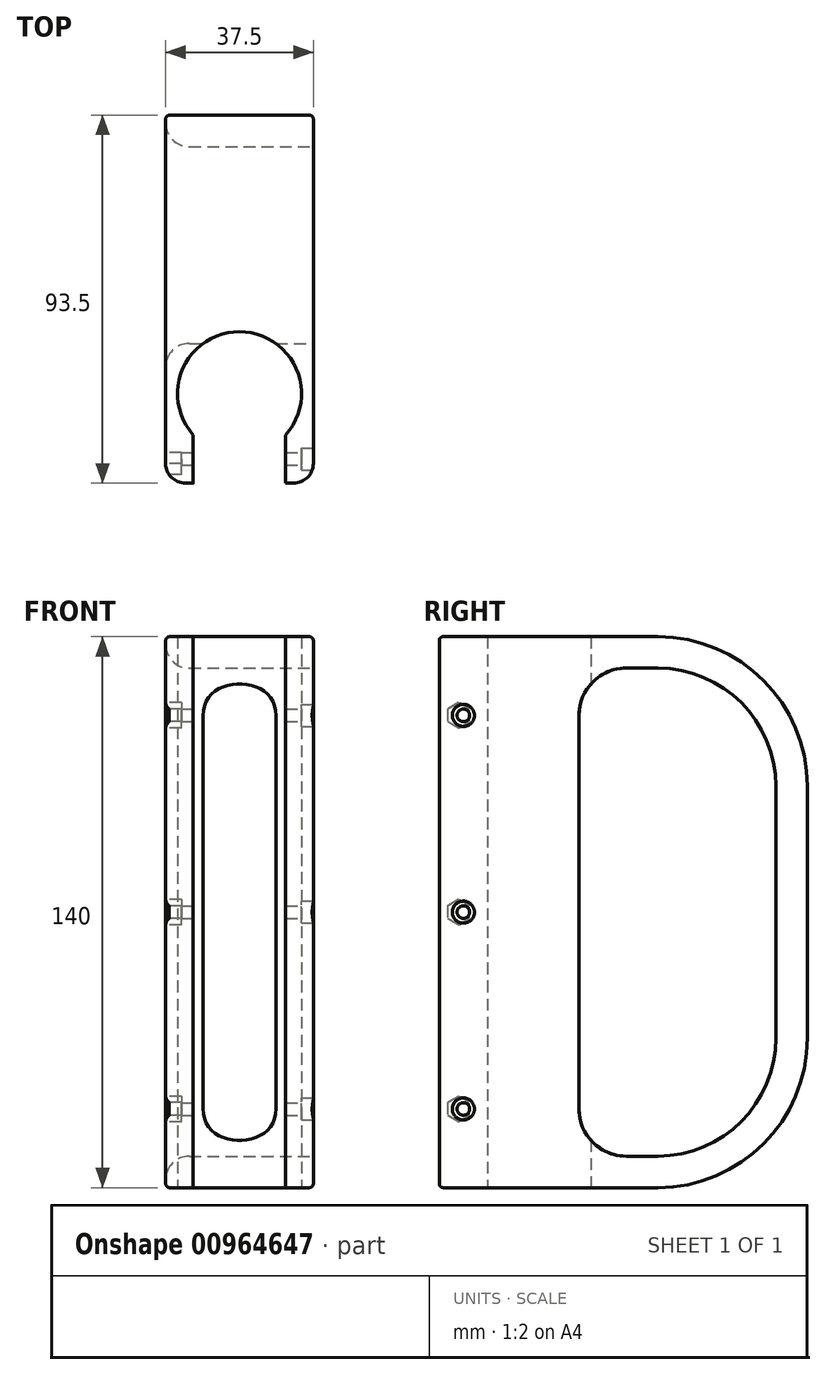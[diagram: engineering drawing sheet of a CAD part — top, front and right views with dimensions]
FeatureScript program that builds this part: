
annotation { "Feature Type Name" : "Feature", "Feature Type Description" : "" }
export const myFeature = defineFeature(function(context is Context, id is Id, definition is map)
    precondition{}
    {
        {
            var Q0;
            Q0=qCreatedBy(makeId("Top.planeOp"),FACE);
            var sketch = newSketch(context, id + "F0", { "sketchPlane" : qUnion([Q0])});
            skCircle(sketch, "E0", {"center": v(0, 0) * mm, "radius": 15.75 * mm});
            skSolve(sketch);
        }
        {
            var Q0;
            Q0=qCreatedBy(makeId("Top.planeOp"),FACE);
            var sketch = newSketch(context, id + "F1", { "sketchPlane" : qUnion([Q0])});
            skLineSegment(sketch, "E1", {"start": v(0, 70.75) * mm, "end": v(18.75, 70.75) * mm});
            skLineSegment(sketch, "E2", {"start": v(18.75, 70.75) * mm, "end": v(18.75, -22.75) * mm});
            skLineSegment(sketch, "E3", {"start": v(18.75, -22.75) * mm, "end": v(11.75, -22.75) * mm});
            skLineSegment(sketch, "E4", {"start": v(11.75, -22.75) * mm, "end": v(11.75, -10.49) * mm});
            skArc(sketch, "E5", {"start": v(11.75, -10.49) * mm, "mid": v(14.37, 6.44) * mm, "end": v(0, 15.75) * mm});
            skLineSegment(sketch, "E6", {"start": v(0, 15.75) * mm, "end": v(0, 70.75) * mm});
            skLineSegment(sketch, "E7", {"start": v(15.75, 0) * mm, "end": v(15.75, -22.75) * mm, "construction": true});
            skLineSegment(sketch, "E8", {"start": v(0, -15.75) * mm, "end": v(11.75, -15.75) * mm, "construction": true});
            skSolve(sketch);
        }
        {
            var Q0;
            Q0=makeQuery(id+"F1.imprint","IMPRINT",FACE,{"disambiguationData":[TD([[makeQuery(id+"F1.imprint","IMPRINT",EDGE,{"derivedFrom":sQuery(id+"F1.wireOp",EDGE,"E1")}),-1.0]])]});
            extrude(context, id + "F2", {"entities" : qUnion([Q0]), "depth" : 70 * mm});
        }
        {
            var Q0;
            Q0=makeQuery(id+"F2.opExtrude","SWEPT_BODY",BODY,{"disambiguationData":[OSD([sQuery(id+"F1.wireOp",EDGE,"E1"),sQuery(id+"F1.wireOp",EDGE,"E2"),sQuery(id+"F1.wireOp",EDGE,"E3"),sQuery(id+"F1.wireOp",EDGE,"E4"),sQuery(id+"F1.wireOp",EDGE,"E5"),sQuery(id+"F1.wireOp",EDGE,"E6")])]});
            var Q1;
            Q1=makeQuery(id+"F2.opExtrude","SWEPT_FACE",FACE,{"disambiguationData":[OSD([sQuery(id+"F1.wireOp",EDGE,"E6")])]});
            mirror(context, id + "F3", {"operationType" : NewBodyOperationType.ADD, "entities" : qUnion([Q0]), "mirrorPlane" : qUnion([Q1])});
        }
        {
            var Q0;
            Q0=makeQuery(id+"F2.opExtrude","SWEPT_FACE",FACE,{"disambiguationData":[OSD([sQuery(id+"F1.wireOp",EDGE,"E2")])]});
            var sketch = newSketch(context, id + "F4", { "sketchPlane" : qUnion([Q0])});
            skLineSegment(sketch, "E9", {"start": v(62.75, 70) * mm, "end": v(62.75, 38) * mm});
            skLineSegment(sketch, "E10", {"start": v(12.75, 20) * mm, "end": v(12.75, 70) * mm});
            skLineSegment(sketch, "E11", {"start": v(62.75, 70) * mm, "end": v(12.75, 70) * mm});
            skLineSegment(sketch, "E12", {"start": v(15.75, 70) * mm, "end": v(15.75, 0) * mm, "construction": true});
            skLineSegment(sketch, "E13", {"start": v(70.75, 8) * mm, "end": v(15.75, 8) * mm, "construction": true});
            skLineSegment(sketch, "E14", {"start": v(32.75, 8) * mm, "end": v(24.75, 8) * mm});
            skArc(sketch, "E15", {"start": v(12.75, 20) * mm, "mid": v(16.26, 11.51) * mm, "end": v(24.75, 8) * mm});
            skArc(sketch, "E16", {"start": v(32.75, 8) * mm, "mid": v(53.96, 16.79) * mm, "end": v(62.75, 38) * mm});
            skSolve(sketch);
        }
        {
            var Q0;
            Q0=qSketchRegion(id+"F4",true);
            var Q1;
            {var subQ2=sQuery(id+"F4.wireOp",EDGE,"E11");Q1=makeQuery(id+"F4.imprint","IMPRINT",FACE,{"disambiguationData":[TD([[makeQuery(id+"F4.imprint","IMPRINT",EDGE,{"derivedFrom":subQ2}),1.0]])]});}
            extrude(context, id + "F5", {"entities" : qUnion([Q0, Q1]), "operationType" : NewBodyOperationType.REMOVE, "endBound" : BoundingType.THROUGH_ALL, "oppositeDirection" : true, "depth" : 25 * mm});
        }
        {
            var Q0;
            {var subQ0=makeQuery(id+"F2.opExtrude","SWEPT_FACE",FACE,{"disambiguationData":[OSD([sQuery(id+"F1.wireOp",EDGE,"E2")])]});Q0=makeQuery(id+"F8.boolean.opBoolean","MERGE",FACE,{"derivedFrom":[subQ0,makeQuery(id+"F8.opPattern","COPY",FACE,{"derivedFrom":subQ0,"instanceName":"1"})]});}
            var sketch = newSketch(context, id + "F6", { "sketchPlane" : qUnion([Q0])});
            skArc(sketch, "E17", {"start": v(32.75, 0) * mm, "mid": v(59.62, 11.13) * mm, "end": v(70.75, 38) * mm});
            skLineSegment(sketch, "E18", {"start": v(70.75, 38) * mm, "end": v(70.75, 0) * mm});
            skLineSegment(sketch, "E19", {"start": v(70.75, 0) * mm, "end": v(32.75, 0) * mm});
            skSolve(sketch);
        }
        {
            var Q0;
            Q0=qSketchRegion(id+"F6",true);
            extrude(context, id + "F7", {"entities" : qUnion([Q0]), "operationType" : NewBodyOperationType.REMOVE, "endBound" : BoundingType.THROUGH_ALL, "oppositeDirection" : true, "depth" : 25 * mm});
        }
        {
            var Q0;
            Q0=makeQuery(id+"F2.opExtrude","SWEPT_BODY",BODY,{"disambiguationData":[OSD([sQuery(id+"F1.wireOp",EDGE,"E1"),sQuery(id+"F1.wireOp",EDGE,"E2"),sQuery(id+"F1.wireOp",EDGE,"E3"),sQuery(id+"F1.wireOp",EDGE,"E4"),sQuery(id+"F1.wireOp",EDGE,"E5"),sQuery(id+"F1.wireOp",EDGE,"E6")])]});
            var Q1;
            {var subQ0=sQuery(id+"F1.wireOp",EDGE,"E2");var subQ1=sQuery(id+"F1.wireOp",EDGE,"E3");var subQ2=sQuery(id+"F1.wireOp",EDGE,"E4");var subQ3=sQuery(id+"F1.wireOp",EDGE,"E5");var subQ4=makeQuery(id+"F2.opExtrude","CAP_FACE",FACE,{"disambiguationData":[OSD([sQuery(id+"F1.wireOp",EDGE,"E1"),subQ0,subQ1,subQ2,subQ3,sQuery(id+"F1.wireOp",EDGE,"E6")])],"isStart":false});var subQ6=makeQuery(id+"F2.opExtrude","SWEPT_FACE",FACE,{"disambiguationData":[OSD([subQ1])]});Q1=makeQuery(id+"F5.boolean.opBoolean","SPLIT",FACE,{"disambiguationData":[TD([subQ6])],"derivedFrom":makeQuery(id+"F3.boolean.opBoolean","MERGE",FACE,{"derivedFrom":[subQ4,makeQuery(id+"F3.opPattern","COPY",FACE,{"derivedFrom":subQ4,"instanceName":"1"})]})});}
            mirror(context, id + "F8", {"operationType" : NewBodyOperationType.ADD, "entities" : qUnion([Q0]), "mirrorPlane" : qUnion([Q1])});
        }
        {
            var Q0;
            {var subQ0=makeQuery(id+"F5.boolean.opBoolean","COPY",EDGE,{"derivedFrom":makeQuery(id+"F5.opExtrude","CAP_EDGE",EDGE,{"disambiguationData":[OSD([sQuery(id+"F4.wireOp",EDGE,"E10")])],"isStart":true})});Q0=makeQuery(id+"F8.boolean.opBoolean","MERGE",EDGE,{"derivedFrom":[subQ0,makeQuery(id+"F8.opPattern","COPY",EDGE,{"derivedFrom":subQ0,"instanceName":"1"})]});}
            var Q1;
            {var subQ0=makeQuery(id+"F5.boolean.opBoolean","INTERSECT",EDGE,{"derivedFrom":[makeQuery(id+"F3.opPattern","COPY",FACE,{"derivedFrom":makeQuery(id+"F2.opExtrude","SWEPT_FACE",FACE,{"disambiguationData":[OSD([sQuery(id+"F1.wireOp",EDGE,"E2")])]}),"instanceName":"1"}),makeQuery(id+"F5.opExtrude","SWEPT_FACE",FACE,{"disambiguationData":[OSD([sQuery(id+"F4.wireOp",EDGE,"E10")])]})]});Q1=makeQuery(id+"F8.boolean.opBoolean","MERGE",EDGE,{"derivedFrom":[subQ0,makeQuery(id+"F8.opPattern","COPY",EDGE,{"derivedFrom":subQ0,"instanceName":"1"})]});}
            fillet(context, id + "F9", {"entities" : qUnion([Q0, Q1]), "radius" : 6 * mm, "tangentPropagation" : true, "allowEdgeOverflow" : false});
        }
        {
            var Q0;
            {var subQ0=makeQuery(id+"F2.opExtrude","SWEPT_FACE",FACE,{"disambiguationData":[OSD([sQuery(id+"F1.wireOp",EDGE,"E2")])]});Q0=makeQuery(id+"F8.boolean.opBoolean","MERGE",FACE,{"derivedFrom":[subQ0,makeQuery(id+"F8.opPattern","COPY",FACE,{"derivedFrom":subQ0,"instanceName":"1"})]});}
            var sketch = newSketch(context, id + "F10", { "sketchPlane" : qUnion([Q0])});
            skCircle(sketch, "E20", {"center": v(-16.62, 20) * mm, "radius": 1.6 * mm});
            skCircle(sketch, "E21", {"center": v(-16.62, 70) * mm, "radius": 1.6 * mm});
            skCircle(sketch, "E22", {"center": v(-16.62, 120) * mm, "radius": 1.6 * mm});
            skLineSegment(sketch, "E23", {"start": v(-16.62, 20) * mm, "end": v(-16.62, 70) * mm, "construction": true});
            skLineSegment(sketch, "E24", {"start": v(-16.62, 70) * mm, "end": v(-16.62, 120) * mm, "construction": true});
            skLineSegment(sketch, "E25", {"start": v(-16.62, 120) * mm, "end": v(-16.62, 140) * mm, "construction": true});
            skLineSegment(sketch, "E26", {"start": v(-16.62, 20) * mm, "end": v(-16.62, 0) * mm, "construction": true});
            skSolve(sketch);
        }
        {
            var Q0;
            Q0=qSketchRegion(id+"F10",true);
            extrude(context, id + "F11", {"entities" : qUnion([Q0]), "operationType" : NewBodyOperationType.REMOVE, "endBound" : BoundingType.THROUGH_ALL, "oppositeDirection" : true, "depth" : 25 * mm});
        }
        {
            var Q0;
            {var subQ0=makeQuery(id+"F2.opExtrude","SWEPT_FACE",FACE,{"disambiguationData":[OSD([sQuery(id+"F1.wireOp",EDGE,"E2")])]});Q0=makeQuery(id+"F8.boolean.opBoolean","MERGE",FACE,{"derivedFrom":[subQ0,makeQuery(id+"F8.opPattern","COPY",FACE,{"derivedFrom":subQ0,"instanceName":"1"})]});}
            var sketch = newSketch(context, id + "F12", { "sketchPlane" : qUnion([Q0])});
            skCircle(sketch, "E27", {"center": v(-16.62, 120) * mm, "radius": 2.8 * mm});
            skCircle(sketch, "E28", {"center": v(-16.62, 70) * mm, "radius": 2.8 * mm});
            skCircle(sketch, "E29", {"center": v(-16.62, 20) * mm, "radius": 2.8 * mm});
            skSolve(sketch);
        }
        {
            var Q0;
            Q0=qSketchRegion(id+"F12",true);
            extrude(context, id + "F13", {"entities" : qUnion([Q0]), "operationType" : NewBodyOperationType.REMOVE, "oppositeDirection" : true, "depth" : 3 * mm});
        }
        {
            var Q0;
            {var subQ0=makeQuery(id+"F3.opPattern","COPY",FACE,{"derivedFrom":makeQuery(id+"F2.opExtrude","SWEPT_FACE",FACE,{"disambiguationData":[OSD([sQuery(id+"F1.wireOp",EDGE,"E2")])]}),"instanceName":"1"});Q0=makeQuery(id+"F8.boolean.opBoolean","MERGE",FACE,{"derivedFrom":[subQ0,makeQuery(id+"F8.opPattern","COPY",FACE,{"derivedFrom":subQ0,"instanceName":"1"})]});}
            var sketch = newSketch(context, id + "F14", { "sketchPlane" : qUnion([Q0])});
            skLineSegment(sketch, "E30", {"start": v(15, 68.38) * mm, "end": v(15, 71.62) * mm});
            skLineSegment(sketch, "E31", {"start": v(15, 71.62) * mm, "end": v(17.8, 73.23) * mm});
            skLineSegment(sketch, "E32", {"start": v(17.8, 73.23) * mm, "end": v(20.6, 71.62) * mm});
            skLineSegment(sketch, "E33", {"start": v(20.6, 71.62) * mm, "end": v(20.6, 68.38) * mm});
            skLineSegment(sketch, "E34", {"start": v(20.6, 68.38) * mm, "end": v(17.8, 66.77) * mm});
            skLineSegment(sketch, "E35", {"start": v(17.8, 66.77) * mm, "end": v(15, 68.38) * mm});
            skLineSegment(sketch, "E36", {"start": v(15, 118.38) * mm, "end": v(15, 121.62) * mm});
            skLineSegment(sketch, "E37", {"start": v(15, 121.62) * mm, "end": v(17.8, 123.23) * mm});
            skLineSegment(sketch, "E38", {"start": v(17.8, 123.23) * mm, "end": v(20.6, 121.62) * mm});
            skLineSegment(sketch, "E39", {"start": v(20.6, 121.62) * mm, "end": v(20.6, 118.38) * mm});
            skLineSegment(sketch, "E40", {"start": v(20.6, 118.38) * mm, "end": v(17.8, 116.77) * mm});
            skLineSegment(sketch, "E41", {"start": v(17.8, 116.77) * mm, "end": v(15, 118.38) * mm});
            skLineSegment(sketch, "E42", {"start": v(15, 18.38) * mm, "end": v(15, 21.62) * mm});
            skLineSegment(sketch, "E43", {"start": v(15, 21.62) * mm, "end": v(17.8, 23.23) * mm});
            skLineSegment(sketch, "E44", {"start": v(17.8, 23.23) * mm, "end": v(20.6, 21.62) * mm});
            skLineSegment(sketch, "E45", {"start": v(20.6, 21.62) * mm, "end": v(20.6, 18.38) * mm});
            skLineSegment(sketch, "E46", {"start": v(20.6, 18.38) * mm, "end": v(17.8, 16.77) * mm});
            skLineSegment(sketch, "E47", {"start": v(17.8, 16.77) * mm, "end": v(15, 18.38) * mm});
            skCircle(sketch, "E48", {"center": v(17.8, 20) * mm, "radius": 3.23 * mm, "construction": true});
            skCircle(sketch, "E49", {"center": v(17.8, 70) * mm, "radius": 3.23 * mm, "construction": true});
            skCircle(sketch, "E50", {"center": v(17.8, 120) * mm, "radius": 3.23 * mm, "construction": true});
            skSolve(sketch);
        }
        {
            var Q0;
            Q0=makeQuery(id+"F14.imprint","IMPRINT",FACE,{"disambiguationData":[TD([[makeQuery(id+"F14.imprint","IMPRINT",EDGE,{"derivedFrom":sQuery(id+"F14.wireOp",EDGE,"E42")}),-1.0]])]});
            var Q1;
            Q1=makeQuery(id+"F14.imprint","IMPRINT",FACE,{"disambiguationData":[TD([[makeQuery(id+"F14.imprint","IMPRINT",EDGE,{"derivedFrom":sQuery(id+"F14.wireOp",EDGE,"E30")}),-1.0]])]});
            var Q2;
            Q2=makeQuery(id+"F14.imprint","IMPRINT",FACE,{"disambiguationData":[TD([[makeQuery(id+"F14.imprint","IMPRINT",EDGE,{"derivedFrom":sQuery(id+"F14.wireOp",EDGE,"E36")}),-1.0]])]});
            extrude(context, id + "F15", {"entities" : qUnion([Q0, Q1, Q2]), "operationType" : NewBodyOperationType.REMOVE, "oppositeDirection" : true, "depth" : 4 * mm});
        }
        {
            var Q0;
            {var subQ0=makeQuery(id+"F2.opExtrude","SWEPT_EDGE",EDGE,{"disambiguationData":[OSD([sQuery(id+"F1.wireOp",EDGE,"E2"),sQuery(id+"F1.wireOp",EDGE,"E3")])]});Q0=makeQuery(id+"F8.boolean.opBoolean","MERGE",EDGE,{"derivedFrom":[subQ0,makeQuery(id+"F8.opPattern","COPY",EDGE,{"derivedFrom":subQ0,"instanceName":"1"})]});}
            var Q1;
            {var subQ0=makeQuery(id+"F3.opPattern","COPY",EDGE,{"derivedFrom":makeQuery(id+"F2.opExtrude","SWEPT_EDGE",EDGE,{"disambiguationData":[OSD([sQuery(id+"F1.wireOp",EDGE,"E2"),sQuery(id+"F1.wireOp",EDGE,"E3")])]}),"instanceName":"1"});Q1=makeQuery(id+"F8.boolean.opBoolean","MERGE",EDGE,{"derivedFrom":[subQ0,makeQuery(id+"F8.opPattern","COPY",EDGE,{"derivedFrom":subQ0,"instanceName":"1"})]});}
            fillet(context, id + "F16", {"entities" : qUnion([Q0, Q1]), "radius" : 5 * mm, "tangentPropagation" : true, "allowEdgeOverflow" : false});
        }
        {
            var Q0;
            Q0=makeQuery(id+"F3.opPattern","COPY",EDGE,{"derivedFrom":makeQuery(id+"F2.opExtrude","CAP_EDGE",EDGE,{"disambiguationData":[OSD([sQuery(id+"F1.wireOp",EDGE,"E2")])],"isStart":true}),"instanceName":"1"});
            var Q1;
            {var subQ0=makeQuery(id+"F5.boolean.opBoolean","INTERSECT",EDGE,{"derivedFrom":[makeQuery(id+"F3.opPattern","COPY",FACE,{"derivedFrom":makeQuery(id+"F2.opExtrude","SWEPT_FACE",FACE,{"disambiguationData":[OSD([sQuery(id+"F1.wireOp",EDGE,"E2")])]}),"instanceName":"1"}),makeQuery(id+"F5.opExtrude","SWEPT_FACE",FACE,{"disambiguationData":[OSD([sQuery(id+"F4.wireOp",EDGE,"E9")])]})]});var subQ1=makeQuery(id+"F2.opExtrude","SWEPT_FACE",FACE,{"disambiguationData":[OSD([sQuery(id+"F1.wireOp",EDGE,"E1")])]});var subQ2=makeQuery(id+"F3.boolean.opBoolean","MERGE",FACE,{"derivedFrom":[subQ1,makeQuery(id+"F3.opPattern","COPY",FACE,{"derivedFrom":subQ1,"instanceName":"1"})]});Q1=makeQuery(id+"F9.opFillet","BLEND_EDGE",EDGE,{"blendedFrom":[makeQuery(id+"F8.boolean.opBoolean","MERGE",EDGE,{"derivedFrom":[subQ0,makeQuery(id+"F8.opPattern","COPY",EDGE,{"derivedFrom":subQ0,"instanceName":"1"})]}),makeQuery(id+"F8.boolean.opBoolean","MERGE",FACE,{"derivedFrom":[subQ2,makeQuery(id+"F8.opPattern","COPY",FACE,{"derivedFrom":subQ2,"instanceName":"1"})]})],"blendedInto":[makeQuery(id+"F8.boolean.opBoolean","MERGE",FACE,{"derivedFrom":[subQ2,makeQuery(id+"F8.opPattern","COPY",FACE,{"derivedFrom":subQ2,"instanceName":"1"})]})]});}
            var Q2;
            Q2=makeQuery(id+"F8.opPattern","COPY",EDGE,{"derivedFrom":makeQuery(id+"F2.opExtrude","CAP_EDGE",EDGE,{"disambiguationData":[OSD([sQuery(id+"F1.wireOp",EDGE,"E2")])],"isStart":true}),"instanceName":"1"});
            fillet(context, id + "F17", {"entities" : qUnion([Q0, Q1, Q2]), "radius" : 1 * mm, "tangentPropagation" : true, "allowEdgeOverflow" : false});
        }
    });
